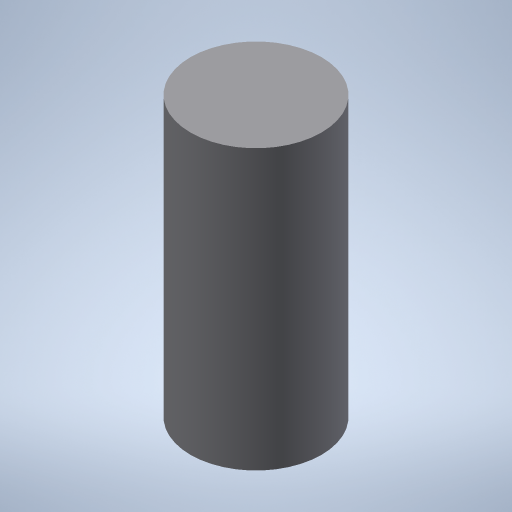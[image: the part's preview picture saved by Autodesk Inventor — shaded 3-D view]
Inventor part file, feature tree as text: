
AUTODESK INVENTOR PART (.ipt)
format: ipt  version: 2024 (Build 280153000, 153)  size: 337,408 bytes
history: native  units: mm
features: extrude x12, sketch x7, projected_geometry x5, fillet x4
ambient origin geometry x8: Origin, YZ Plane, XZ Plane, XY Plane, X Axis, Y Axis, Z Axis, Center Point
bodies: Solid1 (feature_tree)
feature tree (28):
  extrude  "Extrusion1"  Depth=5.0mm
  fillet  "Fillet1"  Radius=5.0mm
  extrude  "Extrusion2"  Depth=21.1mm
  fillet  "Fillet2"  Radius=3.0mm
  extrude  "Extrusion3"  Depth=3.0mm
  extrude  "Extrusion4"  Depth=31.0mm
  extrude  "Extrusion5"  Depth=31.0mm
  fillet  "Fillet3"  Radius=31.0mm
  extrude  "Extrusion6"  Depth=5.6mm
  fillet  "Fillet4"  Radius=9.8mm
  extrude  "Extrusion7"  Depth=31.0mm TaperAngle=0.0deg
  extrude  "Extrusion8"  Depth=0.25mm
  extrude  "Extrusion9"  Depth=7.75mm TaperAngle=0.0deg
  extrude  "Extrusion10"  Depth=32.0mm
  extrude  "Extrusion11"  Depth=0.6mm TaperAngle=0.0deg
  extrude  "Extrusion12"  Depth=22.0mm
  sketch  "Sketch1"  dims[d8=5.0mm d9=5.0mm d10=5.0mm]
  sketch  "Sketch7"  dims[d11=21.1mm d12=21.1mm d13=3.0mm]
  sketch  "Sketch8"  dims[d14=3.0mm d15=3.0mm]
  sketch  "Sketch9"  dims[d16=3.0mm d17=31.0mm]
  projected_geometry  "Projected Loop1"
  sketch  "Sketch10"  dims[d18=31.0mm d19=31.0mm d20=31.0mm]
  projected_geometry  "Projected Loop2"
  projected_geometry  "Projected Loop3"
  sketch  "Sketch12"  dims[d21=5.6mm d22=5.6mm d23=9.8mm d24=0.0mm]
  projected_geometry  "Projected Loop6"
  sketch  "Sketch13"  dims[d25=0.25mm d26=31.0mm d27=0.0mm d28=0.25mm d29=7.75mm d30=0.0mm d31=32.0mm d33=0.6mm d34=0.0mm d35=22.0mm d37=2.2mm d38=0.0mm d39=0.5mm d40=22.5mm d41=0.0mm d42=0.5mm d43=5.6mm d44=5.6mm d45=5.6mm d46=5.6mm d47=42.2mm d48=15.0mm d49=0.0mm d50=9.525mm d51=12.7mm d52=0.0mm d53=12.7mm d54=0.0mm d55=72.8mm d56=0.0mm d57=16.7mm d58=0.0mm d59=5.08mm d60=0.0mm]
  projected_geometry  "Projected Loop7"
